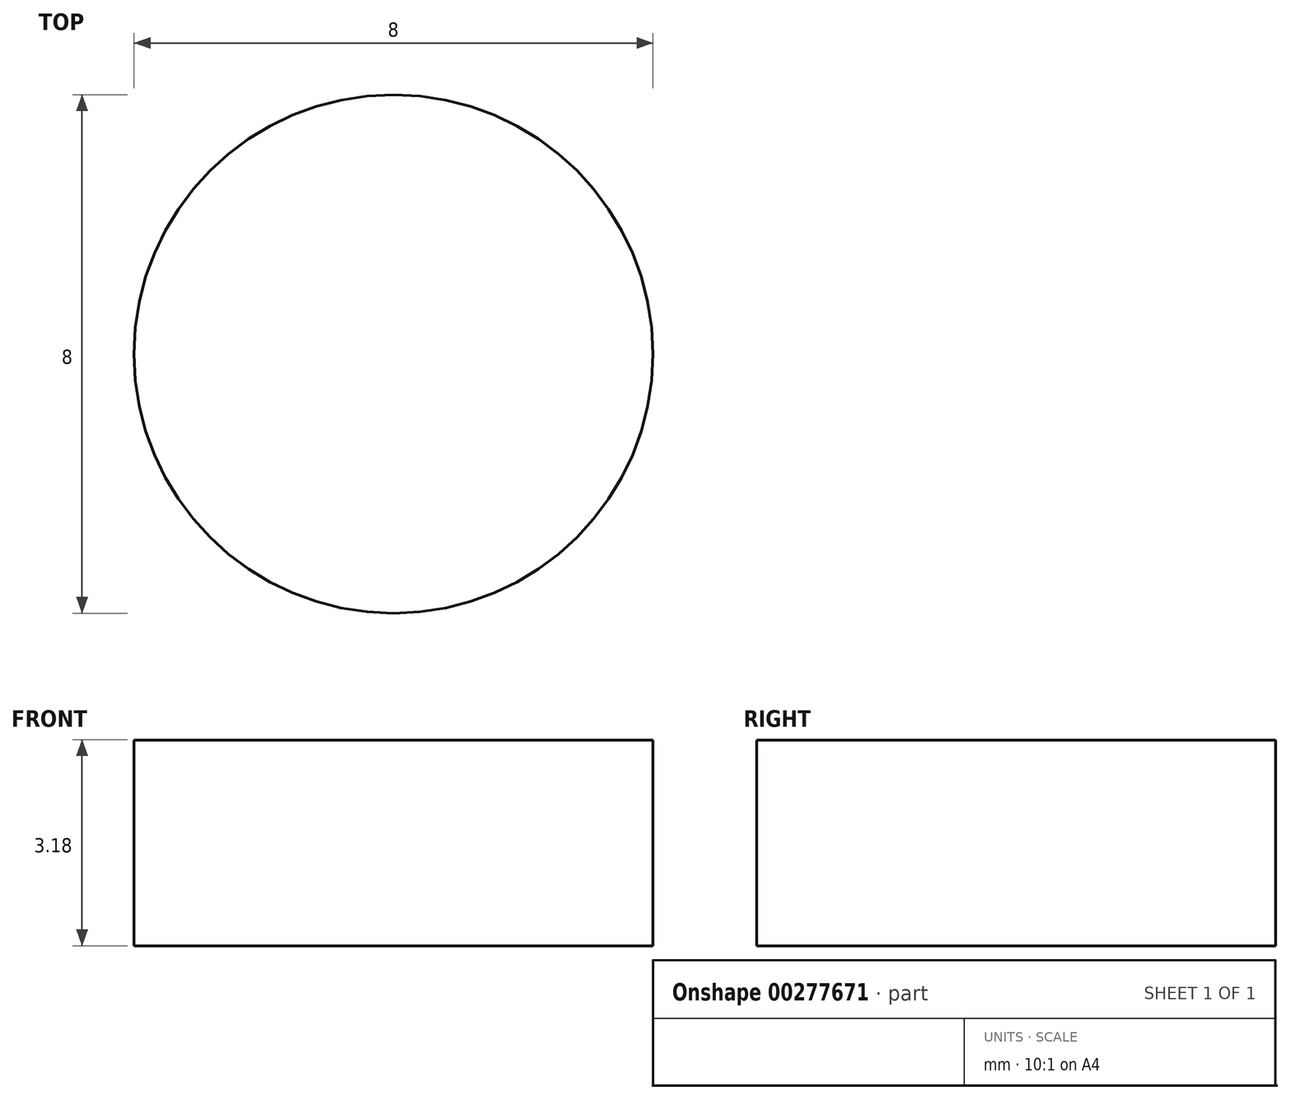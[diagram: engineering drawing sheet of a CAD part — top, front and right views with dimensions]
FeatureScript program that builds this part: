
annotation { "Feature Type Name" : "Feature", "Feature Type Description" : "" }
export const myFeature = defineFeature(function(context is Context, id is Id, definition is map)
    precondition{}
    {
        {
            var Q0;
            Q0=qCreatedBy(makeId("Top.planeOp"),FACE);
            var sketch = newSketch(context, id + "F0", { "sketchPlane" : qUnion([Q0])});
            skCircle(sketch, "E0", {"center": v(0, 0) * mm, "radius": 4 * mm});
            skSolve(sketch);
        }
        {
            var Q0;
            Q0 = qSketchRegion(id + "F0", true);
            extrude(context, id + "F1", {"entities" : qUnion([Q0]), "depth" : 3.17 * mm});
        }
    });
